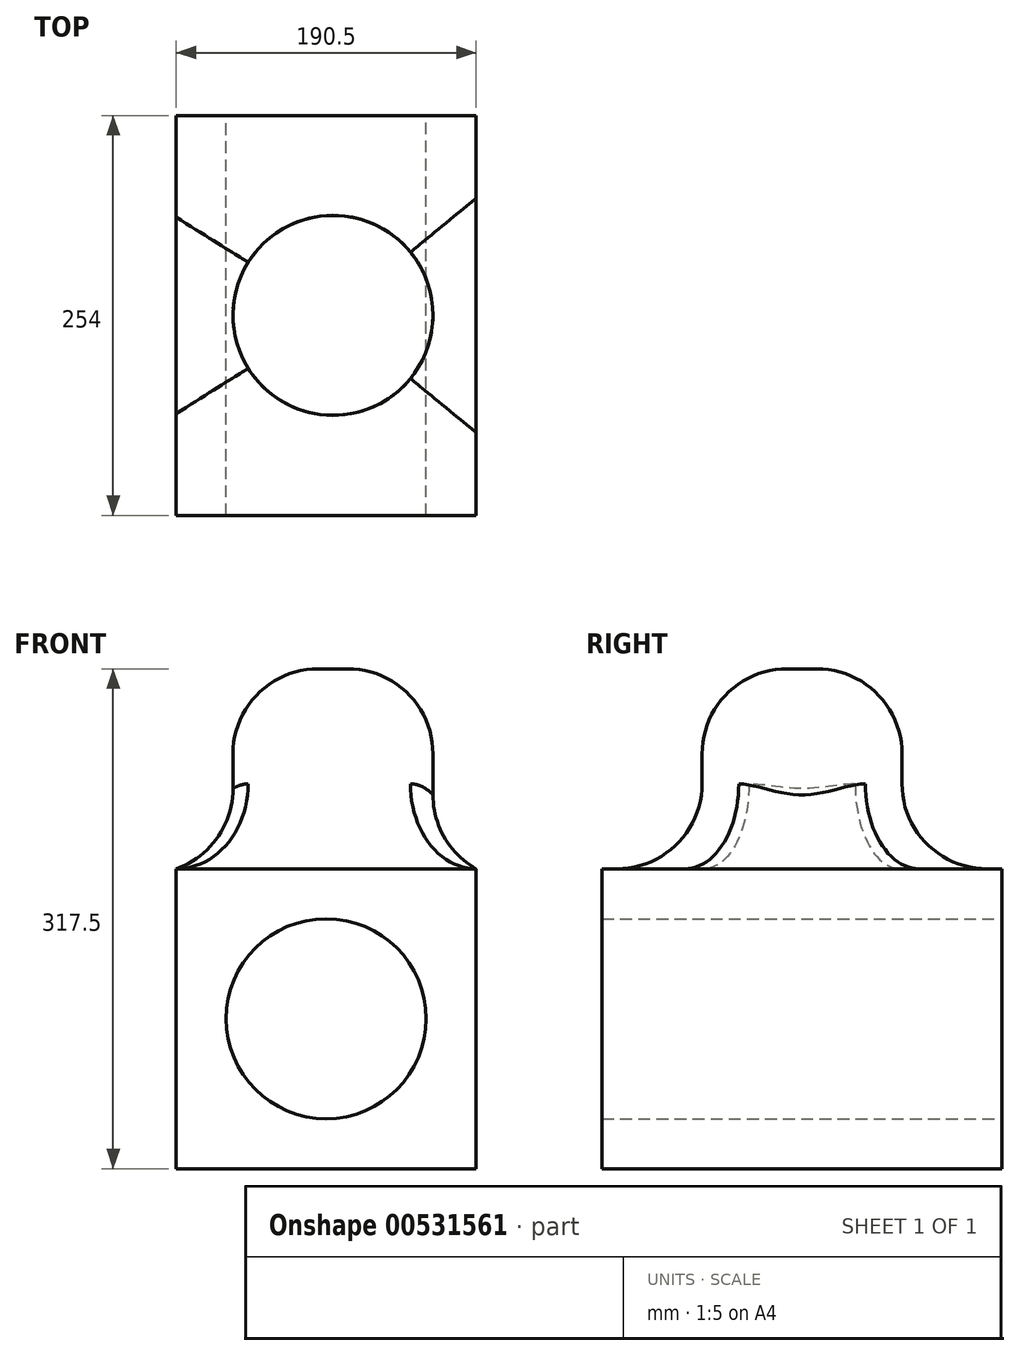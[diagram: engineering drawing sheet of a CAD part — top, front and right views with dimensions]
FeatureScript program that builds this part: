
annotation { "Feature Type Name" : "Feature", "Feature Type Description" : "" }
export const myFeature = defineFeature(function(context is Context, id is Id, definition is map)
    precondition{}
    {
        {
            var Q0;
            Q0=qCreatedBy(makeId("Front.planeOp"),FACE);
            var sketch = newSketch(context, id + "F0", { "sketchPlane" : qUnion([Q0])});
            skLineSegment(sketch, "E0.bottom", {"start": v(-127, 127) * mm, "end": v(127, 127) * mm});
            skLineSegment(sketch, "E0.top", {"start": v(-127, -127) * mm, "end": v(127, -127) * mm});
            skLineSegment(sketch, "E0.left", {"start": v(-127, 127) * mm, "end": v(-127, -127) * mm});
            skLineSegment(sketch, "E0.right", {"start": v(127, 127) * mm, "end": v(127, -127) * mm});
            skPoint(sketch, "E0.middle", {"position": v(0, 0) * mm});
            skCircle(sketch, "E1", {"center": v(0, 0) * mm, "radius": 63.5 * mm});
            skLineSegment(sketch, "E2.bottom", {"start": v(-95.25, 95.25) * mm, "end": v(95.25, 95.25) * mm});
            skLineSegment(sketch, "E2.top", {"start": v(-95.25, -95.25) * mm, "end": v(95.25, -95.25) * mm});
            skLineSegment(sketch, "E2.left", {"start": v(-95.25, 95.25) * mm, "end": v(-95.25, -95.25) * mm});
            skLineSegment(sketch, "E2.right", {"start": v(95.25, 95.25) * mm, "end": v(95.25, -95.25) * mm});
            skSolve(sketch);
        }
        {
            var Q0;
            Q0=makeQuery(id+"F0.imprint","IMPRINT",FACE,{"disambiguationData":[TD([[makeQuery(id+"F0.imprint","IMPRINT",EDGE,{"derivedFrom":sQuery(id+"F0.wireOp",EDGE,"E1")}),-1.0]])]});
            extrude(context, id + "F1", {"entities" : qUnion([Q0]), "endBound" : BoundingType.SYMMETRIC, "depth" : 254 * mm, "offsetDistance" : 25.4 * mm});
        }
        {
            var Q0;
            Q0=makeQuery(id+"F1.opExtrude","SWEPT_FACE",FACE,{"disambiguationData":[OSD([sQuery(id+"F0.wireOp",EDGE,"E2.bottom")])]});
            var sketch = newSketch(context, id + "F2", { "sketchPlane" : qUnion([Q0])});
            skCircle(sketch, "E3", {"center": v(4.32, 0) * mm, "radius": 63.5 * mm});
            skSolve(sketch);
        }
        {
            var Q0;
            Q0 = qSketchRegion(id + "F2", true);
            extrude(context, id + "F3", {"entities" : qUnion([Q0]), "operationType" : NewBodyOperationType.ADD, "depth" : 127 * mm, "offsetDistance" : 25.4 * mm});
        }
        {
            var Q0;
            Q0=makeQuery(id+"F3.opExtrude","SWEPT_FACE",FACE,{"disambiguationData":[OSD([sQuery(id+"F2.wireOp",EDGE,"E3")])]});
            fillet(context, id + "F4", {"entities" : qUnion([Q0]), "radius" : 53.96 * mm, "tangentPropagation" : true, "allowEdgeOverflow" : false});
        }
    });
